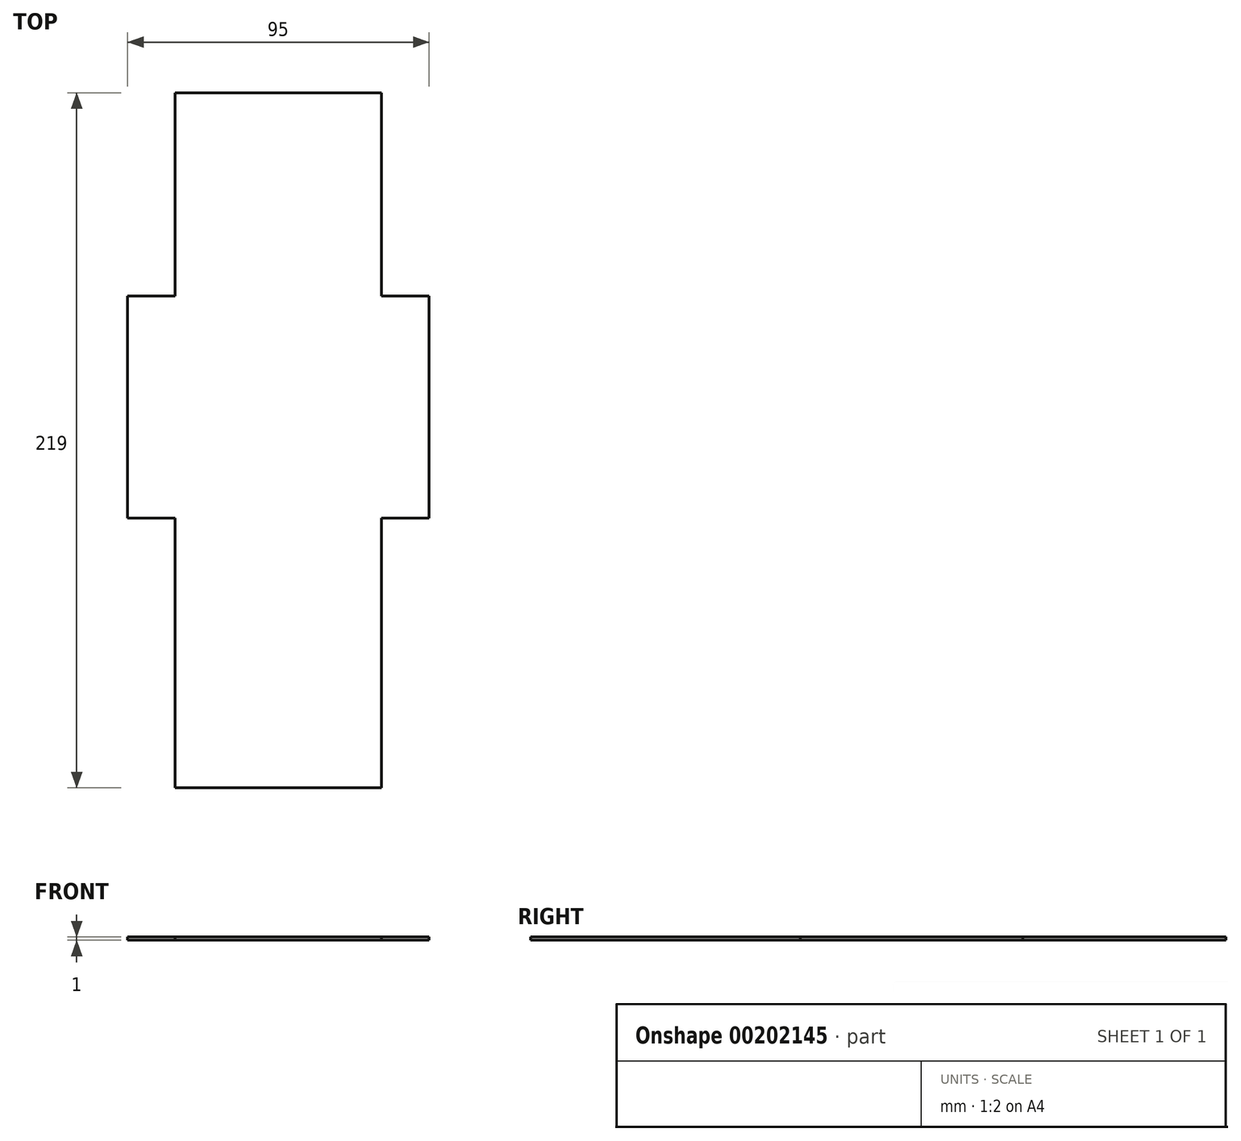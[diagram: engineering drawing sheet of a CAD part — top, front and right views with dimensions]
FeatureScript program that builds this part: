
annotation { "Feature Type Name" : "Feature", "Feature Type Description" : "" }
export const myFeature = defineFeature(function(context is Context, id is Id, definition is map)
    precondition{}
    {
        {
            var Q0;
            Q0=qCreatedBy(makeId("Top.planeOp"),FACE);
            var sketch = newSketch(context, id + "F0", { "sketchPlane" : qUnion([Q0])});
            skLineSegment(sketch, "E0.bottom", {"start": v(32.5, -35) * mm, "end": v(-32.5, -35) * mm});
            skLineSegment(sketch, "E0.top", {"start": v(32.5, 35) * mm, "end": v(-32.5, 35) * mm});
            skLineSegment(sketch, "E0.left", {"start": v(32.5, -35) * mm, "end": v(32.5, 35) * mm});
            skLineSegment(sketch, "E0.right", {"start": v(-32.5, -35) * mm, "end": v(-32.5, 35) * mm});
            skPoint(sketch, "E0.middle", {"position": v(0, 0) * mm});
            skLineSegment(sketch, "E1.bottom", {"start": v(-32.5, 35) * mm, "end": v(32.5, 35) * mm});
            skLineSegment(sketch, "E1.top", {"start": v(-32.5, 80) * mm, "end": v(32.5, 80) * mm});
            skLineSegment(sketch, "E1.left", {"start": v(-32.5, 35) * mm, "end": v(-32.5, 80) * mm});
            skLineSegment(sketch, "E1.right", {"start": v(32.5, 35) * mm, "end": v(32.5, 80) * mm});
            skLineSegment(sketch, "E2.bottom", {"start": v(-32.5, -35) * mm, "end": v(32.5, -35) * mm});
            skLineSegment(sketch, "E2.top", {"start": v(-32.5, -80) * mm, "end": v(32.5, -80) * mm});
            skLineSegment(sketch, "E2.left", {"start": v(-32.5, -35) * mm, "end": v(-32.5, -80) * mm});
            skLineSegment(sketch, "E2.right", {"start": v(32.5, -35) * mm, "end": v(32.5, -80) * mm});
            skLineSegment(sketch, "E3.top", {"start": v(-32.5, 99) * mm, "end": v(32.5, 99) * mm});
            skLineSegment(sketch, "E3.left", {"start": v(-32.5, 80) * mm, "end": v(-32.5, 99) * mm});
            skLineSegment(sketch, "E3.right", {"start": v(32.5, 80) * mm, "end": v(32.5, 99) * mm});
            skLineSegment(sketch, "E4.top", {"start": v(-32.5, -105) * mm, "end": v(32.5, -105) * mm});
            skLineSegment(sketch, "E4.left", {"start": v(-32.5, -80) * mm, "end": v(-32.5, -105) * mm});
            skLineSegment(sketch, "E4.right", {"start": v(32.5, -80) * mm, "end": v(32.5, -105) * mm});
            skLineSegment(sketch, "E5.top", {"start": v(-32.5, -120) * mm, "end": v(32.5, -120) * mm});
            skLineSegment(sketch, "E5.left", {"start": v(-32.5, -105) * mm, "end": v(-32.5, -120) * mm});
            skLineSegment(sketch, "E5.right", {"start": v(32.5, -105) * mm, "end": v(32.5, -120) * mm});
            skLineSegment(sketch, "E6.bottom", {"start": v(-32.5, -35) * mm, "end": v(-47.5, -35) * mm});
            skLineSegment(sketch, "E6.top", {"start": v(-32.5, 35) * mm, "end": v(-47.5, 35) * mm});
            skLineSegment(sketch, "E6.right", {"start": v(-47.5, -35) * mm, "end": v(-47.5, 35) * mm});
            skLineSegment(sketch, "E7.bottom", {"start": v(32.5, 35) * mm, "end": v(47.5, 35) * mm});
            skLineSegment(sketch, "E7.top", {"start": v(32.5, -35) * mm, "end": v(47.5, -35) * mm});
            skLineSegment(sketch, "E7.left", {"start": v(32.5, 35) * mm, "end": v(32.5, -35) * mm});
            skLineSegment(sketch, "E7.right", {"start": v(47.5, 35) * mm, "end": v(47.5, -35) * mm});
            skSolve(sketch);
        }
        {
            var Q0;
            Q0 = qSketchRegion(id + "F0", true);
            extrude(context, id + "F1", {"entities" : qUnion([Q0]), "depth" : 1 * mm});
        }
    });
